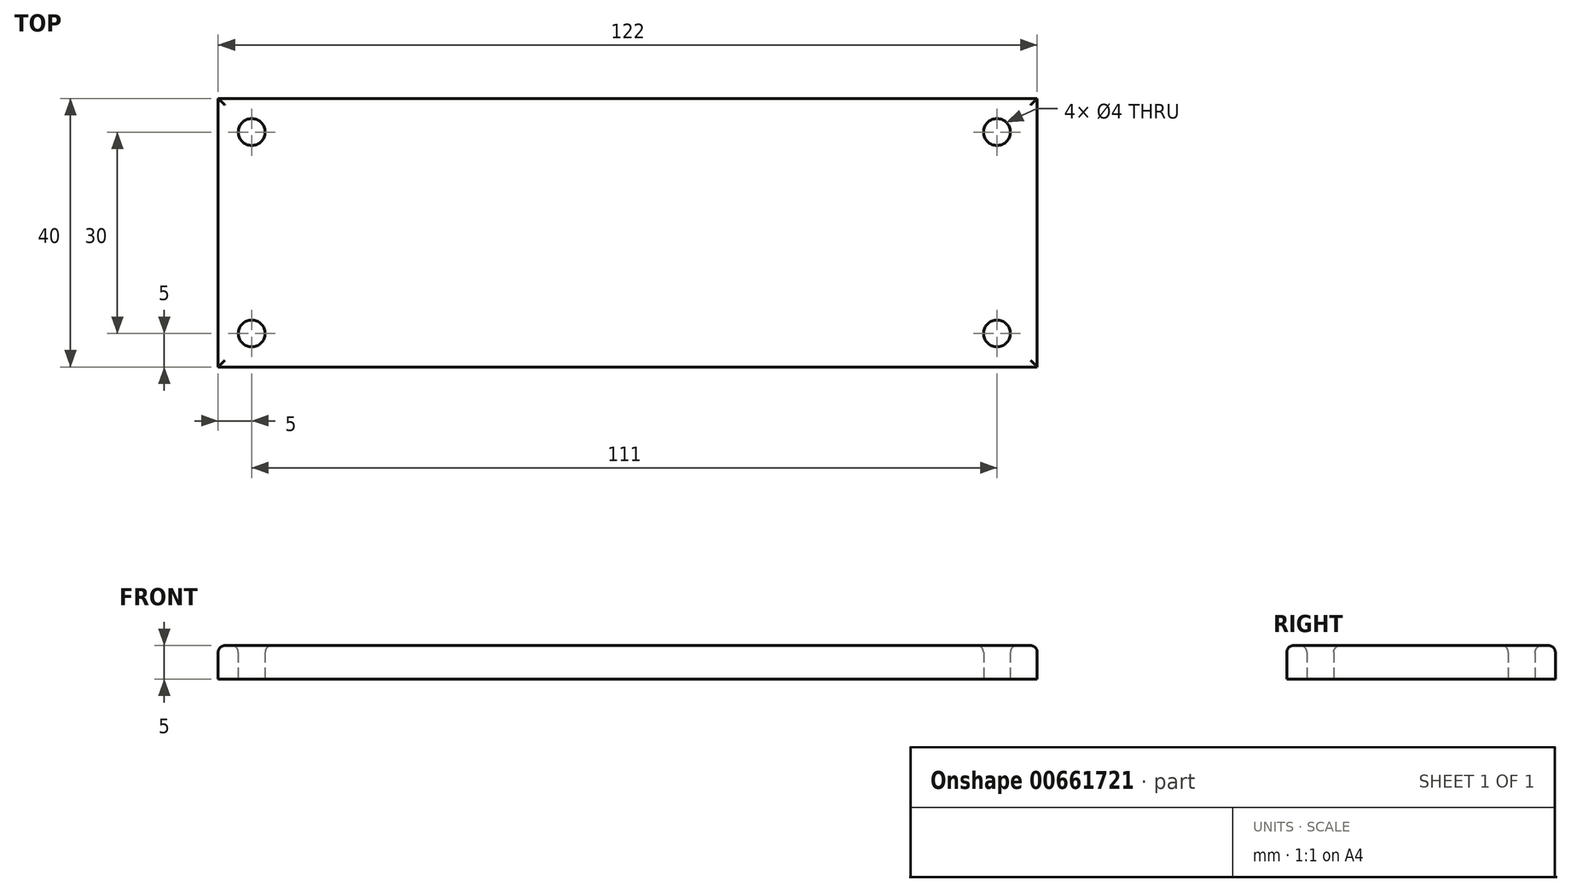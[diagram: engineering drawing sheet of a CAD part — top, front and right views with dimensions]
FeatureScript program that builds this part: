
annotation { "Feature Type Name" : "Feature", "Feature Type Description" : "" }
export const myFeature = defineFeature(function(context is Context, id is Id, definition is map)
    precondition{}
    {
        {
            var Q0;
            Q0=qCreatedBy(makeId("Top.planeOp"),FACE);
            var sketch = newSketch(context, id + "F0", { "sketchPlane" : qUnion([Q0])});
            skLineSegment(sketch, "E0.bottom", {"start": v(-61, 20) * mm, "end": v(61, 20) * mm});
            skLineSegment(sketch, "E0.top", {"start": v(-61, -20) * mm, "end": v(61, -20) * mm});
            skLineSegment(sketch, "E0.left", {"start": v(-61, 20) * mm, "end": v(-61, -20) * mm});
            skLineSegment(sketch, "E0.right", {"start": v(61, 20) * mm, "end": v(61, -20) * mm});
            skPoint(sketch, "E0.middle", {"position": v(0, 0) * mm});
            skCircle(sketch, "E1", {"center": v(-56, -15) * mm, "radius": 2 * mm});
            skCircle(sketch, "E2.1.0.0", {"center": v(55, -15) * mm, "radius": 2 * mm});
            skLineSegment(sketch, "E2.direction1", {"start": v(-56, -15) * mm, "end": v(55, -15) * mm, "construction": true});
            skCircle(sketch, "E3", {"center": v(-56, 15) * mm, "radius": 2 * mm});
            skCircle(sketch, "E4.1.0.0", {"center": v(55, 15) * mm, "radius": 2 * mm});
            skLineSegment(sketch, "E4.direction1", {"start": v(-56, 15) * mm, "end": v(55, 15) * mm, "construction": true});
            skSolve(sketch);
        }
        {
            var Q0;
            Q0 = qSketchRegion(id + "F0", true);
            extrude(context, id + "F1", {"entities" : qUnion([Q0]), "depth" : 5 * mm, "offsetDistance" : 25 * mm});
        }
        {
            var Q0;
            Q0=makeQuery(id+"F1.opExtrude","CAP_FACE",FACE,{"disambiguationData":[OSD([sQuery(id+"F0.wireOp",EDGE,"E0.bottom"),sQuery(id+"F0.wireOp",EDGE,"E0.top"),sQuery(id+"F0.wireOp",EDGE,"E0.left"),sQuery(id+"F0.wireOp",EDGE,"E0.right"),sQuery(id+"F0.wireOp",EDGE,"E1"),sQuery(id+"F0.wireOp",EDGE,"E2.1.0.0"),sQuery(id+"F0.wireOp",EDGE,"E3"),sQuery(id+"F0.wireOp",EDGE,"E4.1.0.0")])],"isStart":false});
            fillet(context, id + "F2", {"entities" : qUnion([Q0]), "radius" : 1 * mm, "tangentPropagation" : true, "allowEdgeOverflow" : false});
        }
    });
